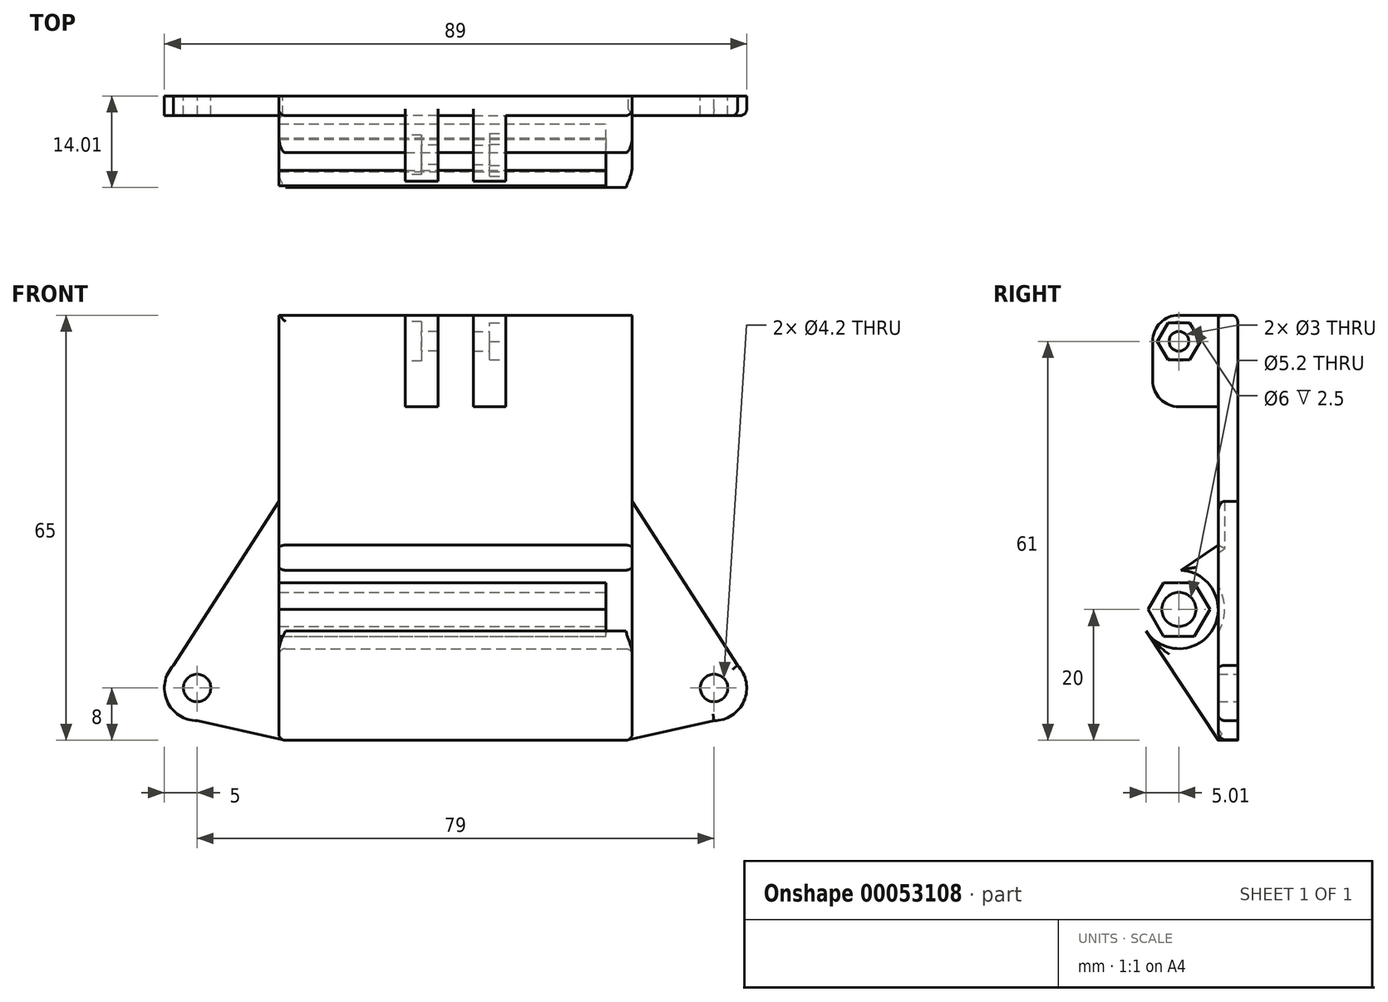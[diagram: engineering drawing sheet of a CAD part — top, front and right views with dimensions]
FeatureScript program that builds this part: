
annotation { "Feature Type Name" : "Feature", "Feature Type Description" : "" }
export const myFeature = defineFeature(function(context is Context, id is Id, definition is map)
    precondition{}
    {
        {
            var Q0;
            Q0=qCreatedBy(makeId("Top.planeOp"),FACE);
            var sketch = newSketch(context, id + "F0", { "sketchPlane" : qUnion([Q0])});
            skLineSegment(sketch, "E0.bottom", {"start": v(-27, 0) * mm, "end": v(27, 0) * mm});
            skLineSegment(sketch, "E0.top", {"start": v(-27, -3) * mm, "end": v(27, -3) * mm});
            skLineSegment(sketch, "E0.left", {"start": v(-27, 0) * mm, "end": v(-27, -3) * mm});
            skLineSegment(sketch, "E0.right", {"start": v(27, 0) * mm, "end": v(27, -3) * mm});
            skSolve(sketch);
        }
        {
            var Q0;
            Q0=qSketchRegion(id+"F0",true);
            var Q1;
            Q1=makeQuery(id+"F0.imprint","IMPRINT",FACE,{"disambiguationData":[TD([[makeQuery(id+"F0.imprint","IMPRINT",EDGE,{"derivedFrom":sQuery(id+"F0.wireOp",EDGE,"E0.bottom")}),-1.0]])]});
            extrude(context, id + "F1", {"entities" : qUnion([Q0, Q1]), "depth" : 45 * mm, "hasSecondDirection" : true, "secondDirectionOppositeDirection" : true, "secondDirectionDepth" : 20 * mm});
        }
        {
            var Q0;
            Q0=makeQuery(id+"F1.opExtrude","SWEPT_FACE",FACE,{"disambiguationData":[OSD([sQuery(id+"F0.wireOp",EDGE,"E0.right")])]});
            var sketch = newSketch(context, id + "F2", { "sketchPlane" : qUnion([Q0])});
            skCircle(sketch, "E1", {"center": v(-9, 0) * mm, "radius": 6 * mm});
            skCircle(sketch, "E2", {"center": v(-9, 0) * mm, "radius": 2.6 * mm});
            skLineSegment(sketch, "E3", {"start": v(-3, -20) * mm, "end": v(-14, -3.3) * mm});
            skLineSegment(sketch, "E4", {"start": v(-8.67, 6) * mm, "end": v(-3, 9.84) * mm});
            skCircle(sketch, "E5.cCircle", {"center": v(-9, 0) * mm, "radius": 4.1 * mm, "construction": true});
            skLineSegment(sketch, "E5.0", {"start": v(-6.63, -4.1) * mm, "end": v(-11.37, -4.1) * mm});
            skLineSegment(sketch, "E5.1", {"start": v(-11.37, -4.1) * mm, "end": v(-13.73, 0) * mm});
            skLineSegment(sketch, "E5.2", {"start": v(-13.73, 0) * mm, "end": v(-11.37, 4.1) * mm});
            skLineSegment(sketch, "E5.3", {"start": v(-11.37, 4.1) * mm, "end": v(-6.63, 4.1) * mm});
            skLineSegment(sketch, "E5.4", {"start": v(-6.63, 4.1) * mm, "end": v(-4.27, 0) * mm});
            skLineSegment(sketch, "E5.5", {"start": v(-4.27, 0) * mm, "end": v(-6.63, -4.1) * mm});
            skPoint(sketch, "E5.0.midPoint", {"position": v(-9, -4.1) * mm});
            skSolve(sketch);
        }
        {
            var Q0;
            Q0=makeQuery(id+"F2.imprint","IMPRINT",FACE,{"disambiguationData":[TD([[makeQuery(id+"F2.imprint","IMPRINT",EDGE,{"derivedFrom":sQuery(id+"F2.wireOp",EDGE,"E5.0")}),1.0]])]});
            var Q1;
            {var subQ3=sQuery(id+"F2.wireOp",EDGE,"E4");Q1=makeQuery(id+"F2.imprint","IMPRINT",FACE,{"disambiguationData":[TD([[makeQuery(id+"F2.imprint","IMPRINT",EDGE,{"derivedFrom":subQ3}),-1.0]])]});}
            var Q2;
            Q2=makeQuery(id+"F2.imprint","IMPRINT",FACE,{"disambiguationData":[TD([[makeQuery(id+"F2.imprint","IMPRINT",EDGE,{"derivedFrom":sQuery(id+"F2.wireOp",EDGE,"E2")}),-1.0]])]});
            var Q3;
            {var subQ0=sQuery(id+"F2.wireOp",EDGE,"E3");Q3=makeQuery(id+"F2.imprint","IMPRINT",FACE,{"disambiguationData":[TD([[makeQuery(id+"F2.imprint","IMPRINT",EDGE,{"derivedFrom":subQ0}),-1.0]])]});}
            var Q4;
            Q4=makeQuery(id+"F1.opExtrude","SWEPT_FACE",FACE,{"disambiguationData":[OSD([sQuery(id+"F0.wireOp",EDGE,"E0.left")])]});
            extrude(context, id + "F3", {"entities" : qUnion([Q0, Q1, Q2, Q3]), "operationType" : NewBodyOperationType.ADD, "endBound" : BoundingType.UP_TO_SURFACE, "oppositeDirection" : true, "endBoundEntityFace" : qUnion([Q4]), "depth" : 25 * mm});
        }
        {
            var Q0;
            Q0=makeQuery(id+"F1.opExtrude","SWEPT_FACE",FACE,{"disambiguationData":[OSD([sQuery(id+"F0.wireOp",EDGE,"E0.top")])]});
            var sketch = newSketch(context, id + "F4", { "sketchPlane" : qUnion([Q0])});
            skLineSegment(sketch, "E6.bottom", {"start": v(2.7, 41) * mm, "end": v(7.7, 41) * mm});
            skLineSegment(sketch, "E6.top", {"start": v(2.7, 31) * mm, "end": v(7.7, 31) * mm});
            skLineSegment(sketch, "E6.left", {"start": v(2.7, 41) * mm, "end": v(2.7, 31) * mm});
            skLineSegment(sketch, "E6.right", {"start": v(7.7, 41) * mm, "end": v(7.7, 31) * mm});
            skLineSegment(sketch, "E7.top", {"start": v(2.7, 45) * mm, "end": v(7.7, 45) * mm});
            skLineSegment(sketch, "E7.left", {"start": v(2.7, 41) * mm, "end": v(2.7, 45) * mm});
            skLineSegment(sketch, "E7.right", {"start": v(7.7, 41) * mm, "end": v(7.7, 45) * mm});
            skSolve(sketch);
        }
        {
            var Q0;
            Q0=makeQuery(id+"F4.imprint","IMPRINT",FACE,{"disambiguationData":[TD([[makeQuery(id+"F4.imprint","IMPRINT",EDGE,{"derivedFrom":sQuery(id+"F4.wireOp",EDGE,"E6.top")}),1.0]])]});
            var Q1;
            Q1=makeQuery(id+"F4.imprint","IMPRINT",FACE,{"disambiguationData":[TD([[makeQuery(id+"F4.imprint","IMPRINT",EDGE,{"derivedFrom":sQuery(id+"F4.wireOp",EDGE,"E6.bottom")}),1.0]])]});
            extrude(context, id + "F5", {"entities" : qUnion([Q0, Q1]), "depth" : 10 * mm});
        }
        {
            var Q0;
            Q0=makeQuery(id+"F5.opExtrude","SWEPT_FACE",FACE,{"disambiguationData":[OSD([sQuery(id+"F4.wireOp",EDGE,"E6.right"),sQuery(id+"F4.wireOp",EDGE,"E7.right")])]});
            var sketch = newSketch(context, id + "F6", { "sketchPlane" : qUnion([Q0])});
            skCircle(sketch, "E8", {"center": v(-9, 41) * mm, "radius": 1.5 * mm});
            skCircle(sketch, "E9.cCircle", {"center": v(-9, 41) * mm, "radius": 2.85 * mm, "construction": true});
            skLineSegment(sketch, "E9.0", {"start": v(-10.65, 43.85) * mm, "end": v(-7.35, 43.85) * mm});
            skLineSegment(sketch, "E9.1", {"start": v(-7.35, 43.85) * mm, "end": v(-5.7, 41) * mm});
            skLineSegment(sketch, "E9.2", {"start": v(-5.7, 41) * mm, "end": v(-7.35, 38.15) * mm});
            skLineSegment(sketch, "E9.3", {"start": v(-7.35, 38.15) * mm, "end": v(-10.65, 38.15) * mm});
            skLineSegment(sketch, "E9.4", {"start": v(-10.65, 38.15) * mm, "end": v(-12.3, 41) * mm});
            skLineSegment(sketch, "E9.5", {"start": v(-12.3, 41) * mm, "end": v(-10.65, 43.85) * mm});
            skPoint(sketch, "E9.0.midPoint", {"position": v(-9, 43.85) * mm});
            skSolve(sketch);
        }
        {
            var Q0;
            Q0=makeQuery(id+"F6.imprint","IMPRINT",FACE,{"disambiguationData":[TD([[makeQuery(id+"F6.imprint","IMPRINT",EDGE,{"derivedFrom":sQuery(id+"F6.wireOp",EDGE,"E8")}),1.0]])]});
            extrude(context, id + "F7", {"entities" : qUnion([Q0]), "operationType" : NewBodyOperationType.REMOVE, "oppositeDirection" : true, "depth" : 25 * mm});
        }
        {
            var Q0;
            Q0=makeQuery(id+"F5.opExtrude","SWEPT_BODY",BODY,{"disambiguationData":[OSD([sQuery(id+"F4.wireOp",EDGE,"E6.top"),sQuery(id+"F4.wireOp",EDGE,"E6.left"),sQuery(id+"F4.wireOp",EDGE,"E6.right"),sQuery(id+"F4.wireOp",EDGE,"E7.top"),sQuery(id+"F4.wireOp",EDGE,"E7.left"),sQuery(id+"F4.wireOp",EDGE,"E7.right")])]});
            var Q1;
            Q1=qCreatedBy(makeId("Right.planeOp"),FACE);
            mirror(context, id + "F8", {"operationType" : NewBodyOperationType.ADD, "entities" : qUnion([Q0]), "mirrorPlane" : qUnion([Q1])});
        }
        {
            var Q0;
            Q0=makeQuery(id+"F8.opPattern","COPY",EDGE,{"derivedFrom":makeQuery(id+"F5.opExtrude","CAP_EDGE",EDGE,{"disambiguationData":[OSD([sQuery(id+"F4.wireOp",EDGE,"E7.top")])],"isStart":false}),"instanceName":"1"});
            var Q1;
            Q1=makeQuery(id+"F5.opExtrude","CAP_EDGE",EDGE,{"disambiguationData":[OSD([sQuery(id+"F4.wireOp",EDGE,"E7.top")])],"isStart":false});
            var Q2;
            Q2=makeQuery(id+"F8.opPattern","COPY",EDGE,{"derivedFrom":makeQuery(id+"F5.opExtrude","CAP_EDGE",EDGE,{"disambiguationData":[OSD([sQuery(id+"F4.wireOp",EDGE,"E6.top")])],"isStart":true}),"instanceName":"1"});
            var Q3;
            Q3=makeQuery(id+"F5.opExtrude","CAP_EDGE",EDGE,{"disambiguationData":[OSD([sQuery(id+"F4.wireOp",EDGE,"E6.top")])],"isStart":true});
            var Q4;
            Q4=makeQuery(id+"F5.opExtrude","CAP_EDGE",EDGE,{"disambiguationData":[OSD([sQuery(id+"F4.wireOp",EDGE,"E6.top")])],"isStart":false});
            var Q5;
            Q5=makeQuery(id+"F8.opPattern","COPY",EDGE,{"derivedFrom":makeQuery(id+"F5.opExtrude","CAP_EDGE",EDGE,{"disambiguationData":[OSD([sQuery(id+"F4.wireOp",EDGE,"E6.top")])],"isStart":false}),"instanceName":"1"});
            fillet(context, id + "F9", {"entities" : qUnion([Q0, Q1, Q2, Q3, Q4, Q5]), "radius" : 4 * mm, "tangentPropagation" : true, "allowEdgeOverflow" : false});
        }
        {
            var Q0;
            Q0=makeQuery(id+"F6.imprint","IMPRINT",FACE,{"disambiguationData":[TD([[makeQuery(id+"F6.imprint","IMPRINT",EDGE,{"derivedFrom":sQuery(id+"F6.wireOp",EDGE,"E8")}),-1.0]])]});
            extrude(context, id + "F10", {"entities" : qUnion([Q0]), "operationType" : NewBodyOperationType.REMOVE, "oppositeDirection" : true, "depth" : 2.5 * mm});
        }
        {
            var Q0;
            Q0=makeQuery(id+"F8.opPattern","COPY",FACE,{"derivedFrom":makeQuery(id+"F5.opExtrude","SWEPT_FACE",FACE,{"disambiguationData":[OSD([sQuery(id+"F4.wireOp",EDGE,"E6.right"),sQuery(id+"F4.wireOp",EDGE,"E7.right")])]}),"instanceName":"1"});
            var sketch = newSketch(context, id + "F11", { "sketchPlane" : qUnion([Q0])});
            skCircle(sketch, "E10", {"center": v(9, 41) * mm, "radius": 3 * mm});
            skSolve(sketch);
        }
        {
            var Q0;
            Q0=makeQuery(id+"F11.imprint","IMPRINT",FACE,{"disambiguationData":[TD([[makeQuery(id+"F11.imprint","IMPRINT",EDGE,{"derivedFrom":sQuery(id+"F11.wireOp",EDGE,"E10")}),1.0]])]});
            extrude(context, id + "F12", {"entities" : qUnion([Q0]), "operationType" : NewBodyOperationType.REMOVE, "oppositeDirection" : true, "depth" : 2.5 * mm});
        }
        {
            var Q0;
            Q0=makeQuery(id+"F2.imprint","IMPRINT",FACE,{"disambiguationData":[TD([[makeQuery(id+"F2.imprint","IMPRINT",EDGE,{"derivedFrom":sQuery(id+"F2.wireOp",EDGE,"E2")}),-1.0]])]});
            var Q1;
            {var subQ1=sQuery(id+"F2.wireOp",EDGE,"E5.5");var subQ3=sQuery(id+"F2.wireOp",EDGE,"E5.4");var subQ5=makeQuery(id+"F2.imprint","INTERSECT",VERTEX,{"derivedFrom":[subQ3,subQ1]});Q1=makeQuery(id+"F2.imprint","IMPRINT",FACE,{"disambiguationData":[TD([[makeQuery(id+"F2.imprint","IMPRINT",EDGE,{"disambiguationData":[TD([[subQ5,1.0]])],"derivedFrom":subQ3}),-1.0]])]});}
            extrude(context, id + "F13", {"entities" : qUnion([Q0, Q1]), "operationType" : NewBodyOperationType.REMOVE, "oppositeDirection" : true, "depth" : 4 * mm});
        }
        {
            var Q0;
            {var subQ0=sQuery(id+"F0.wireOp",EDGE,"E0.top");var subQ2=sQuery(id+"F0.wireOp",EDGE,"E0.left");Q0=makeQuery(id+"F8.boolean.opBoolean","SPLIT",EDGE,{"disambiguationData":[TD([makeQuery(id+"F1.opExtrude","SWEPT_FACE",FACE,{"disambiguationData":[OSD([subQ2])]})])],"derivedFrom":makeQuery(id+"F1.opExtrude","CAP_EDGE",EDGE,{"disambiguationData":[OSD([subQ0])],"isStart":false})});}
            var Q1;
            {var subQ0=sQuery(id+"F0.wireOp",EDGE,"E0.top");var subQ2=makeQuery(id+"F5.opExtrude","SWEPT_FACE",FACE,{"disambiguationData":[OSD([sQuery(id+"F4.wireOp",EDGE,"E6.left"),sQuery(id+"F4.wireOp",EDGE,"E7.left")])]});Q1=makeQuery(id+"F8.boolean.opBoolean","SPLIT",EDGE,{"disambiguationData":[TD([subQ2])],"derivedFrom":makeQuery(id+"F1.opExtrude","CAP_EDGE",EDGE,{"disambiguationData":[OSD([subQ0])],"isStart":false})});}
            var Q2;
            Q2=makeQuery(id+"F1.opExtrude","CAP_EDGE",EDGE,{"disambiguationData":[OSD([sQuery(id+"F0.wireOp",EDGE,"E0.bottom")])],"isStart":false});
            var Q3;
            Q3=makeQuery(id+"F1.opExtrude","SWEPT_EDGE",EDGE,{"disambiguationData":[OSD([sQuery(id+"F0.wireOp",EDGE,"E0.top"),sQuery(id+"F0.wireOp",EDGE,"E0.right")])]});
            var Q4;
            Q4=makeQuery(id+"F1.opExtrude","SWEPT_EDGE",EDGE,{"disambiguationData":[OSD([sQuery(id+"F0.wireOp",EDGE,"E0.top"),sQuery(id+"F0.wireOp",EDGE,"E0.left")])]});
            var Q5;
            Q5=makeQuery(id+"F3.opExtrude","CAP_EDGE",EDGE,{"disambiguationData":[OSD([sQuery(id+"F2.wireOp",EDGE,"E4")])],"isStart":false});
            var Q6;
            Q6=makeQuery(id+"F3.opExtrude","CAP_EDGE",EDGE,{"disambiguationData":[OSD([sQuery(id+"F2.wireOp",EDGE,"E1")])],"isStart":false});
            var Q7;
            Q7=makeQuery(id+"F3.opExtrude","CAP_EDGE",EDGE,{"disambiguationData":[OSD([sQuery(id+"F2.wireOp",EDGE,"E1")])],"isStart":true});
            var Q8;
            Q8=makeQuery(id+"F3.opExtrude","CAP_EDGE",EDGE,{"disambiguationData":[OSD([sQuery(id+"F2.wireOp",EDGE,"E4")])],"isStart":true});
            var Q9;
            Q9=makeQuery(id+"F3.opExtrude","CAP_EDGE",EDGE,{"disambiguationData":[OSD([sQuery(id+"F2.wireOp",EDGE,"E3")])],"isStart":true});
            var Q10;
            Q10=makeQuery(id+"F1.opExtrude","CAP_EDGE",EDGE,{"disambiguationData":[OSD([sQuery(id+"F0.wireOp",EDGE,"E0.right")])],"isStart":true});
            var Q11;
            Q11=makeQuery(id+"F1.opExtrude","CAP_EDGE",EDGE,{"disambiguationData":[OSD([sQuery(id+"F0.wireOp",EDGE,"E0.left")])],"isStart":true});
            var Q12;
            Q12=makeQuery(id+"F9.opFillet","BLEND_EDGE",EDGE,{"blendedFrom":[makeQuery(id+"F8.opPattern","COPY",EDGE,{"derivedFrom":makeQuery(id+"F5.opExtrude","CAP_EDGE",EDGE,{"disambiguationData":[OSD([sQuery(id+"F4.wireOp",EDGE,"E6.top")])],"isStart":true}),"instanceName":"1"}),makeQuery(id+"F8.opPattern","COPY",FACE,{"derivedFrom":makeQuery(id+"F5.opExtrude","SWEPT_FACE",FACE,{"disambiguationData":[OSD([sQuery(id+"F4.wireOp",EDGE,"E6.right"),sQuery(id+"F4.wireOp",EDGE,"E7.right")])]}),"instanceName":"1"})],"blendedInto":[makeQuery(id+"F8.opPattern","COPY",FACE,{"derivedFrom":makeQuery(id+"F5.opExtrude","SWEPT_FACE",FACE,{"disambiguationData":[OSD([sQuery(id+"F4.wireOp",EDGE,"E6.right"),sQuery(id+"F4.wireOp",EDGE,"E7.right")])]}),"instanceName":"1"})]});
            var Q13;
            Q13=makeQuery(id+"F9.opFillet","BLEND_EDGE",EDGE,{"blendedFrom":[makeQuery(id+"F5.opExtrude","CAP_EDGE",EDGE,{"disambiguationData":[OSD([sQuery(id+"F4.wireOp",EDGE,"E6.top")])],"isStart":true}),makeQuery(id+"F5.opExtrude","SWEPT_FACE",FACE,{"disambiguationData":[OSD([sQuery(id+"F4.wireOp",EDGE,"E6.right"),sQuery(id+"F4.wireOp",EDGE,"E7.right")])]})],"blendedInto":[makeQuery(id+"F5.opExtrude","SWEPT_FACE",FACE,{"disambiguationData":[OSD([sQuery(id+"F4.wireOp",EDGE,"E6.right"),sQuery(id+"F4.wireOp",EDGE,"E7.right")])]})]});
            var Q14;
            Q14=makeQuery(id+"F5.opExtrude","CAP_EDGE",EDGE,{"disambiguationData":[OSD([sQuery(id+"F4.wireOp",EDGE,"E6.right"),sQuery(id+"F4.wireOp",EDGE,"E7.right")])],"isStart":true});
            var Q15;
            Q15=makeQuery(id+"F8.opPattern","COPY",EDGE,{"derivedFrom":makeQuery(id+"F5.opExtrude","CAP_EDGE",EDGE,{"disambiguationData":[OSD([sQuery(id+"F4.wireOp",EDGE,"E6.right"),sQuery(id+"F4.wireOp",EDGE,"E7.right")])],"isStart":true}),"instanceName":"1"});
            fillet(context, id + "F14", {"entities" : qUnion([Q0, Q1, Q2, Q3, Q4, Q5, Q6, Q7, Q8, Q9, Q10, Q11, Q12, Q13, Q14, Q15]), "radius" : 1 * mm, "tangentPropagation" : true, "allowEdgeOverflow" : false});
        }
        {
            var Q0;
            Q0=makeQuery(id+"F1.opExtrude","SWEPT_FACE",FACE,{"disambiguationData":[OSD([sQuery(id+"F0.wireOp",EDGE,"E0.bottom")])]});
            var sketch = newSketch(context, id + "F15", { "sketchPlane" : qUnion([Q0])});
            skCircle(sketch, "E11", {"center": v(-39.5, -12) * mm, "radius": 2.1 * mm});
            skCircle(sketch, "E12", {"center": v(-39.5, -12) * mm, "radius": 4 * mm});
            skCircle(sketch, "E13", {"center": v(-39.5, -12) * mm, "radius": 5 * mm});
            skLineSegment(sketch, "E14", {"start": v(-39.47, -17) * mm, "end": v(-26, -20) * mm});
            skLineSegment(sketch, "E15", {"start": v(-27, -8.66) * mm, "end": v(-34.52, -11.6) * mm});
            skLineSegment(sketch, "E16", {"start": v(-43.11, -8.54) * mm, "end": v(-27, 16.54) * mm});
            skLineSegment(sketch, "E17", {"start": v(-36.94, -7.7) * mm, "end": v(-27, 9.34) * mm});
            skLineSegment(sketch, "E18", {"start": v(-31.97, 0.82) * mm, "end": v(-31.97, -10.61) * mm});
            skSolve(sketch);
        }
        {
            var Q0;
            {var subQ9=sQuery(id+"F15.wireOp",EDGE,"f43fbf14-aad3-40e0-8205-aaed35de7fc1");Q0=makeQuery(id+"F15.imprint","IMPRINT",FACE,{"disambiguationData":[TD([[makeQuery(id+"F15.imprint","IMPRINT",EDGE,{"derivedFrom":subQ9}),1.0]])]});}
            var Q1;
            Q1=makeQuery(id+"F15.imprint","IMPRINT",FACE,{"disambiguationData":[TD([[makeQuery(id+"F15.imprint","IMPRINT",EDGE,{"derivedFrom":sQuery(id+"F15.wireOp",EDGE,"E12")}),-1.0]])]});
            var Q2;
            {var subQ3=sQuery(id+"F15.wireOp",EDGE,"E16");Q2=makeQuery(id+"F15.imprint","IMPRINT",FACE,{"disambiguationData":[TD([[makeQuery(id+"F15.imprint","IMPRINT",EDGE,{"derivedFrom":subQ3}),-1.0]])]});}
            var Q3;
            {var subQ1=sQuery(id+"F15.wireOp",EDGE,"E18");Q3=makeQuery(id+"F15.imprint","IMPRINT",FACE,{"disambiguationData":[TD([[makeQuery(id+"F15.imprint","IMPRINT",EDGE,{"derivedFrom":subQ1}),-1.0]])]});}
            var Q4;
            {var subQ3=sQuery(id+"F15.wireOp",EDGE,"E14");var subQ10=sQuery(id+"F15.wireOp",EDGE,"E13");var subQ12=makeQuery(id+"F15.imprint","INTERSECT",VERTEX,{"derivedFrom":[subQ10,subQ3]});Q4=makeQuery(id+"F15.imprint","IMPRINT",FACE,{"disambiguationData":[TD([[makeQuery(id+"F15.imprint","IMPRINT",EDGE,{"disambiguationData":[TD([[subQ12,-1.0]])],"derivedFrom":subQ10}),-1.0]])]});}
            var Q5;
            {var subQ5=sQuery(id+"F15.wireOp",EDGE,"E18");Q5=makeQuery(id+"F15.imprint","IMPRINT",FACE,{"disambiguationData":[TD([[makeQuery(id+"F15.imprint","IMPRINT",EDGE,{"derivedFrom":subQ5}),1.0]])]});}
            var Q6;
            Q6=makeQuery(id+"F15.imprint","IMPRINT",FACE,{"disambiguationData":[TD([[makeQuery(id+"F15.imprint","IMPRINT",EDGE,{"derivedFrom":sQuery(id+"F15.wireOp",EDGE,"E11")}),-1.0]])]});
            extrude(context, id + "F16", {"entities" : qUnion([Q0, Q1, Q2, Q3, Q4, Q5, Q6]), "oppositeDirection" : true, "depth" : 3 * mm});
        }
        {
            var Q0;
            Q0=makeQuery(id+"F16.opExtrude","SWEPT_BODY",BODY,{"disambiguationData":[OSD([sQuery(id+"F0.wireOp",EDGE,"E0.bottom"),sQuery(id+"F0.wireOp",EDGE,"E0.right"),sQuery(id+"F15.wireOp",EDGE,"E12"),sQuery(id+"F15.wireOp",EDGE,"E13"),sQuery(id+"F15.wireOp",EDGE,"E14"),sQuery(id+"F15.wireOp",EDGE,"E16")])]});
            var Q1;
            Q1=qCreatedBy(makeId("Right.planeOp"),FACE);
            mirror(context, id + "F17", {"operationType" : NewBodyOperationType.ADD, "entities" : qUnion([Q0]), "mirrorPlane" : qUnion([Q1])});
        }
        {
            var Q0;
            Q0=makeQuery(id+"F16.opExtrude","CAP_EDGE",EDGE,{"disambiguationData":[OSD([sQuery(id+"F15.wireOp",EDGE,"E16")])],"isStart":false});
            var Q1;
            Q1=makeQuery(id+"F16.opExtrude","CAP_EDGE",EDGE,{"disambiguationData":[OSD([sQuery(id+"F15.wireOp",EDGE,"E13")])],"isStart":false});
            var Q2;
            Q2=makeQuery(id+"F16.opExtrude","CAP_EDGE",EDGE,{"disambiguationData":[OSD([sQuery(id+"F15.wireOp",EDGE,"E14")])],"isStart":false});
            fillet(context, id + "F18", {"entities" : qUnion([Q0, Q1, Q2]), "radius" : 1 * mm, "tangentPropagation" : true, "allowEdgeOverflow" : false});
        }
    });
